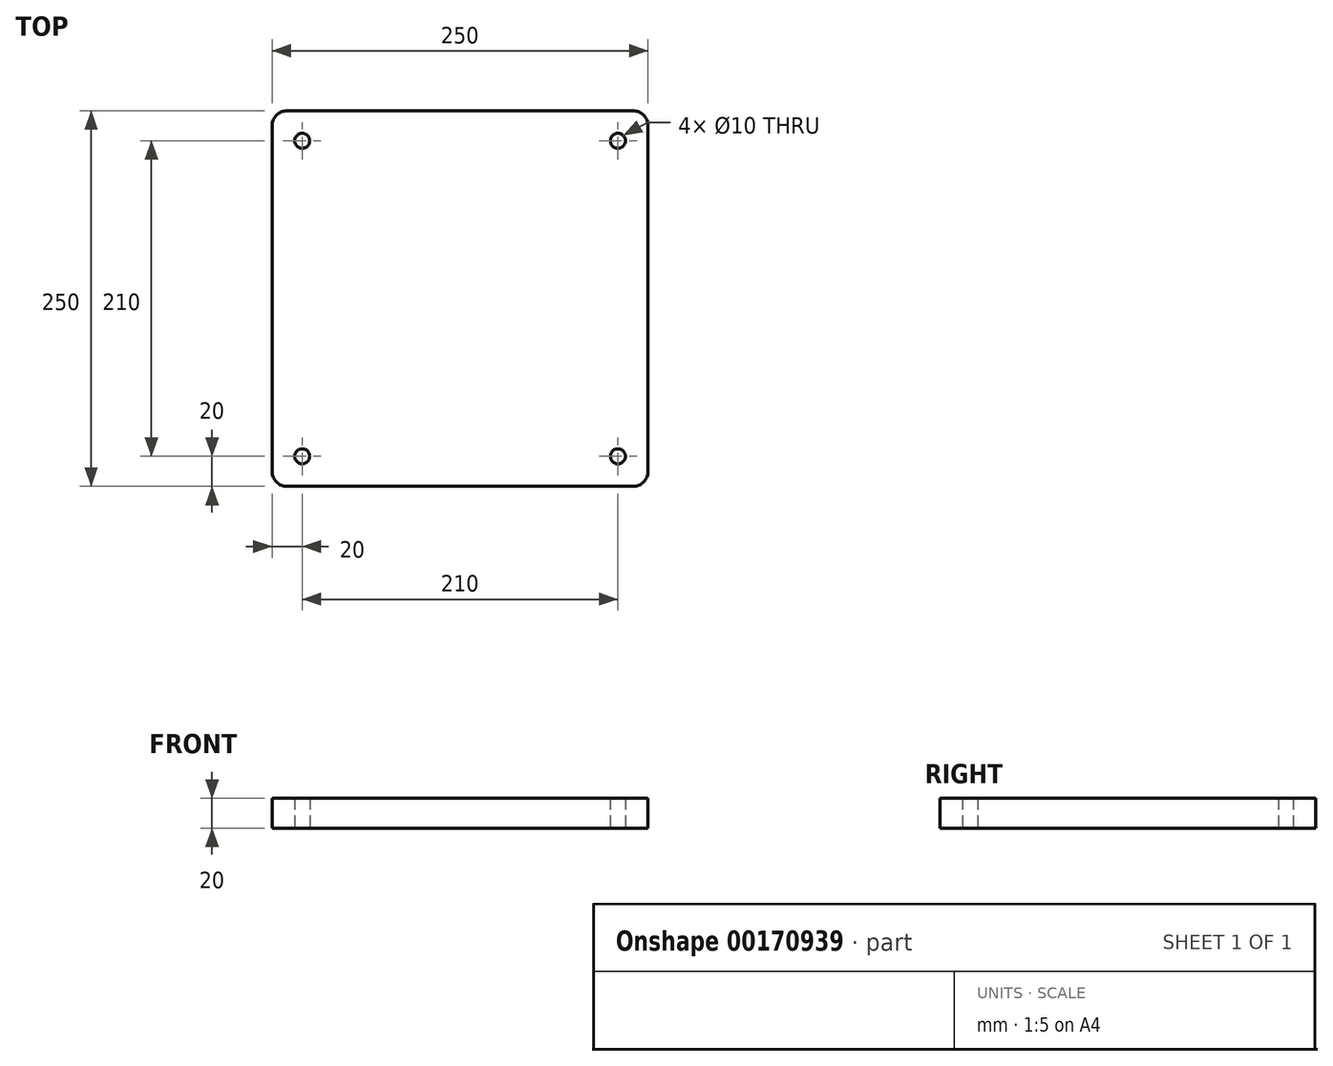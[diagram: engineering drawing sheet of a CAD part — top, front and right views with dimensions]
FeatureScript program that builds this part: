
annotation { "Feature Type Name" : "Feature", "Feature Type Description" : "" }
export const myFeature = defineFeature(function(context is Context, id is Id, definition is map)
    precondition{}
    {
        {
            var Q0;
            Q0=qCreatedBy(makeId("Top.planeOp"),FACE);
            var sketch = newSketch(context, id + "F0", { "sketchPlane" : qUnion([Q0])});
            skLineSegment(sketch, "E0.bottom", {"start": v(10, 0) * mm, "end": v(240, 0) * mm});
            skLineSegment(sketch, "E0.top", {"start": v(10, 250) * mm, "end": v(240, 250) * mm});
            skLineSegment(sketch, "E0.left", {"start": v(0, 10) * mm, "end": v(0, 240) * mm});
            skLineSegment(sketch, "E0.right", {"start": v(250, 10) * mm, "end": v(250, 240) * mm});
            skPoint(sketch, "E1.visualSharp", {"position": v(0, 250) * mm});
            skArc(sketch, "E1.filletArc", {"start": v(10, 250) * mm, "mid": v(2.93, 247.07) * mm, "end": v(0, 240) * mm});
            skPoint(sketch, "E2.visualSharp", {"position": v(250, 250) * mm});
            skArc(sketch, "E2.filletArc", {"start": v(250, 240) * mm, "mid": v(247.07, 247.07) * mm, "end": v(240, 250) * mm});
            skPoint(sketch, "E3.visualSharp", {"position": v(250, 0) * mm});
            skArc(sketch, "E3.filletArc", {"start": v(240, 0) * mm, "mid": v(247.07, 2.93) * mm, "end": v(250, 10) * mm});
            skPoint(sketch, "E4.visualSharp", {"position": v(0, 0) * mm});
            skArc(sketch, "E4.filletArc", {"start": v(0, 10) * mm, "mid": v(2.93, 2.93) * mm, "end": v(10, 0) * mm});
            skCircle(sketch, "E5", {"center": v(20, 230) * mm, "radius": 5 * mm});
            skCircle(sketch, "E6", {"center": v(230, 230) * mm, "radius": 5 * mm});
            skCircle(sketch, "E7", {"center": v(230, 20) * mm, "radius": 5 * mm});
            skCircle(sketch, "E8", {"center": v(20, 20) * mm, "radius": 5 * mm});
            skSolve(sketch);
        }
        {
            var Q0;
            Q0=makeQuery(id+"F0.imprint","IMPRINT",FACE,{"disambiguationData":[TD([[makeQuery(id+"F0.imprint","IMPRINT",EDGE,{"derivedFrom":sQuery(id+"F0.wireOp",EDGE,"E0.bottom")}),1.0]])]});
            extrude(context, id + "F1", {"entities" : qUnion([Q0]), "depth" : 20 * mm, "offsetDistance" : 25 * mm});
        }
    });
